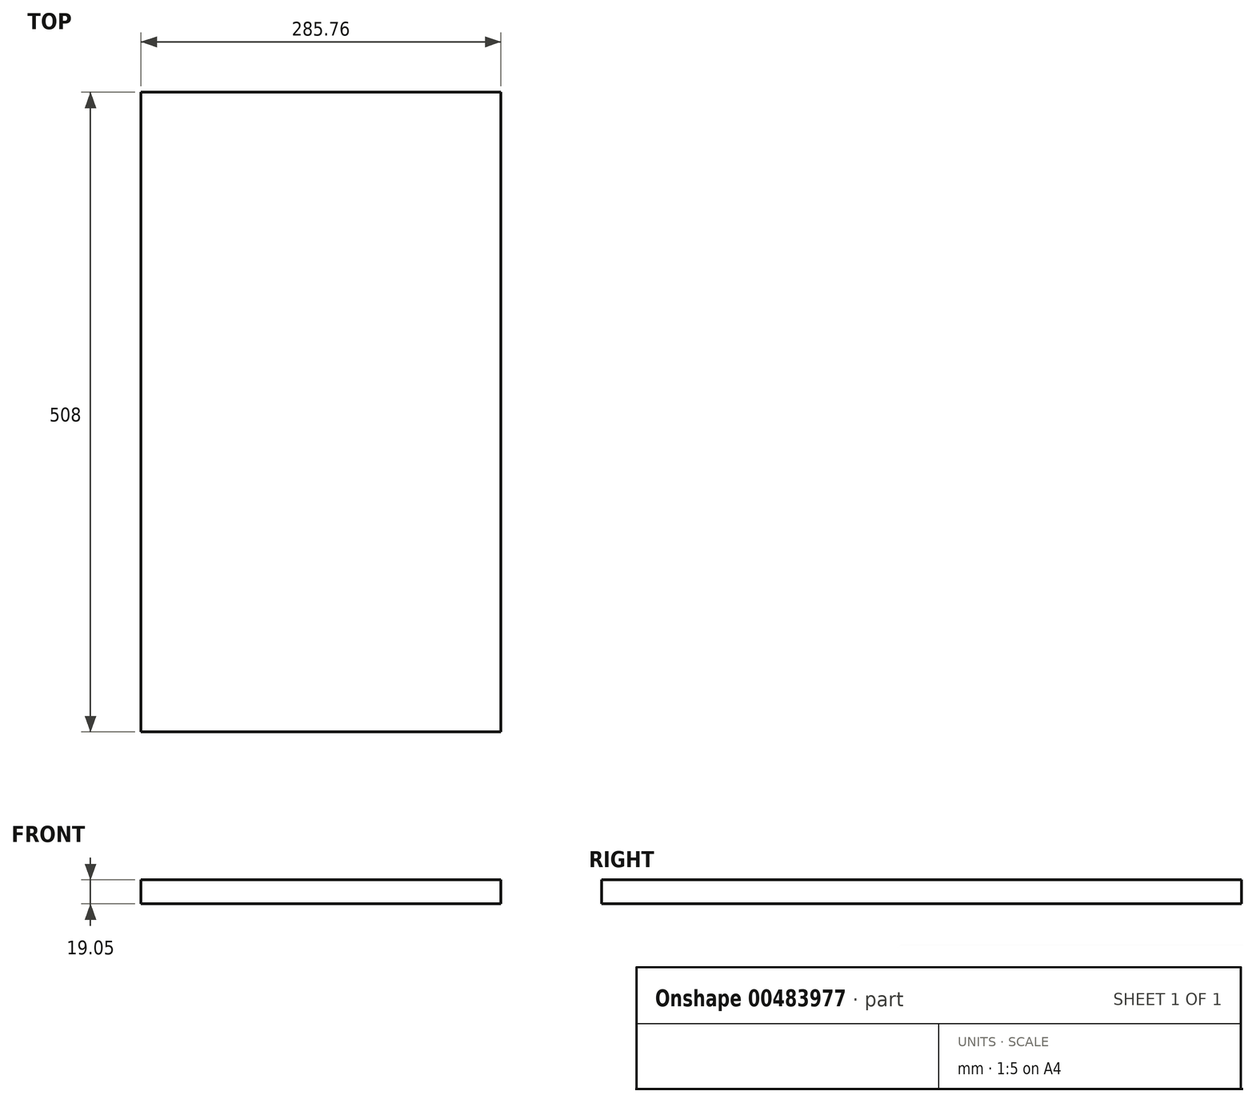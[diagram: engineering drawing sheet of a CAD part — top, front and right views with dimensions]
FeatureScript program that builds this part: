
annotation { "Feature Type Name" : "Feature", "Feature Type Description" : "" }
export const myFeature = defineFeature(function(context is Context, id is Id, definition is map)
    precondition{}
    {
        {
            var Q0;
            Q0=qCreatedBy(makeId("Top.planeOp"),FACE);
            var sketch = newSketch(context, id + "F0", { "sketchPlane" : qUnion([Q0])});
            skLineSegment(sketch, "E0.bottom", {"start": v(142.88, -254) * mm, "end": v(-142.88, -254) * mm});
            skLineSegment(sketch, "E0.top", {"start": v(142.88, 254) * mm, "end": v(-142.88, 254) * mm});
            skLineSegment(sketch, "E0.left", {"start": v(142.88, -254) * mm, "end": v(142.88, 254) * mm});
            skLineSegment(sketch, "E0.right", {"start": v(-142.88, -254) * mm, "end": v(-142.88, 254) * mm});
            skPoint(sketch, "E0.middle", {"position": v(0, 0) * mm});
            skSolve(sketch);
        }
        {
            var Q0;
            Q0 = qSketchRegion(id + "F0", true);
            extrude(context, id + "F1", {"entities" : qUnion([Q0]), "depth" : 19.05 * mm});
        }
    });
